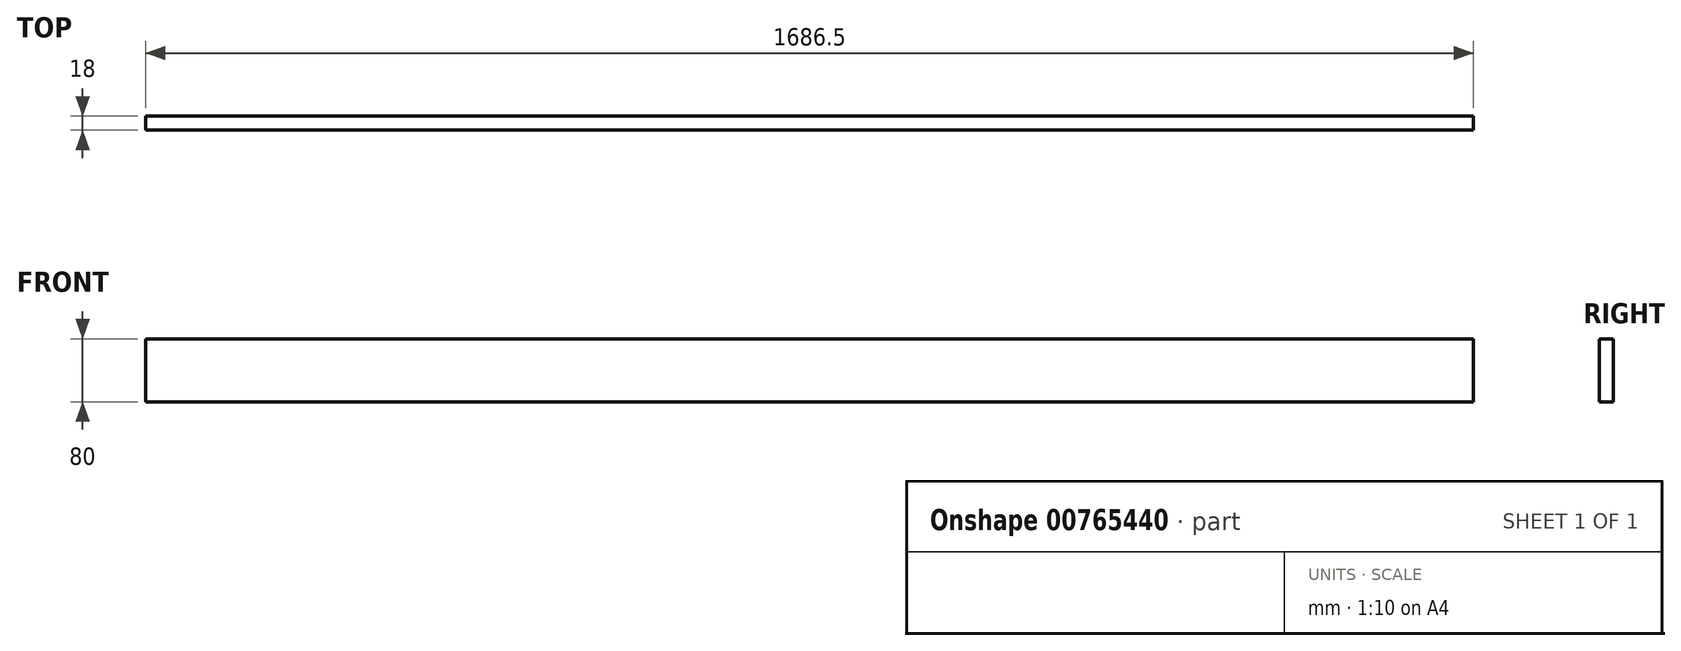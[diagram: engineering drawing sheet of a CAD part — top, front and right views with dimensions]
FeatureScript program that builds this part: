
annotation { "Feature Type Name" : "Feature", "Feature Type Description" : "" }
export const myFeature = defineFeature(function(context is Context, id is Id, definition is map)
    precondition{}
    {
        {
            var Q0;
            Q0=qCreatedBy(makeId("Front.planeOp"),FACE);
            var sketch = newSketch(context, id + "F0", { "sketchPlane" : qUnion([Q0])});
            skLineSegment(sketch, "E0.bottom", {"start": v(-843.25, -40) * mm, "end": v(843.25, -40) * mm});
            skLineSegment(sketch, "E0.top", {"start": v(-843.25, 40) * mm, "end": v(843.25, 40) * mm});
            skLineSegment(sketch, "E0.left", {"start": v(-843.25, -40) * mm, "end": v(-843.25, 40) * mm});
            skLineSegment(sketch, "E0.right", {"start": v(843.25, -40) * mm, "end": v(843.25, 40) * mm});
            skPoint(sketch, "E0.middle", {"position": v(0, 0) * mm});
            skSolve(sketch);
        }
        {
            var Q0;
            Q0 = qSketchRegion(id + "F0", true);
            extrude(context, id + "F1", {"entities" : qUnion([Q0]), "depth" : 18 * mm, "offsetDistance" : 25 * mm});
        }
    });
